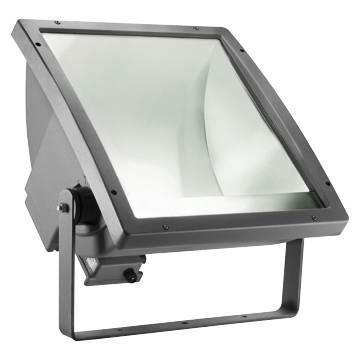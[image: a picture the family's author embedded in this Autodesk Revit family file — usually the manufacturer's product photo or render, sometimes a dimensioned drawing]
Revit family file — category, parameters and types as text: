
# Revit family: Lighting-Proiezione-GEWISS-STADIUM-PROIETTORI_OTTICA_ASIMMETRICA
name_source: partatom
category: Apparecchi per illuminazione
units: mm (PartAtom-declared; Revit-internal decimal feet)

## family parameters
Condiviso = No
Host = Superficie
Numero OmniClass = 23.80.70.00
Punto di calcolo locali = Sì
Quota connettore circolare = Usa diametro
Sorgente d'illuminazione = No
Taglio con vuoti quando caricato = No
Tipo di parte = Normale
Titolo OmniClass = Lighting

## types (2) — shared parameters
Applicazione = Esterno
Attacco lampada = X528/Cavo
Carico apparente = 1000 VA
Catalogo = LIGHTING
Catalogo Serie = STADIUM
Classe isolamento = I
Codice Electrocod = 2433
Colore = Grigio grafite
Commenti sul wattaggio = 1000W
Distanza minima dall'oggetto illuminato = 3M
Grado di protezione = IP66
H_Centro rotazione = 296 mm  [stored 0.971129 ft]
IDF = 25686243-5469-4219-954f-d65ee76d427a
IDT = e7e0fa0a-f0d4-43c6-8d95-65bc926b836b
Immagine tipo = GW84667.jpg
Inquinamento luminoso = 0 cd/Klm
L_interna staffa = 612 mm  [stored 2.00787 ft]
Lampada = MN
Lampada: = MN
Lunghezza proiettore = 604 mm  [stored 1.98163 ft]
Materiale = Alluminio
Numero di poli = 2
Ottica = Asimmetrica - ULOR: 0%
Produttore = GEWISS S.p.A.
Prospetto di default = 1219 mm
Resistenza agli urti = IK09
SEO = Proiettore
Scheda Tecnica = https://www.gewiss.com
Superficie laterale esposta al vento = 0,141M2
Superficie massima esposta al vento = 0,392M2
URL = https://www.gewiss.com
Versione file RFA = 20.11
Voltaggio = 230 V

## per-type parameters (varying)
| type | Codice EAN | Corrente lampada | Corrente lampada: | Descrizione | Modello | Peso (kg) | Peso (kg): | Potenza lampada |
| GW84668 - STADIUM ASI. 2000W MN X528/CAVO | 8011564252325 | 10,3A | 10,3A | STADIUM OTTICA ASIMMETRICA 2000W MN X528/CAVO | GW84668 | 23,5 | 23,5 | 2000W |
| GW84667 - STADIUM ASI. 1000W MN X528/CAVO | 8011564252318 | 9,5A | 9,5A | STADIUM OTTICA ASIMMETRICA 1000W MN X528/CAVO | GW84667 | 24,1 | 24,1 | 1000W |

note: [stored X ft] marks values corroborated as IEEE doubles in the binary element streams (Revit-internal decimal feet)

## geometry (parser evidence)
native form markers: Blend x393
no freeform markers — native parametric forms only
